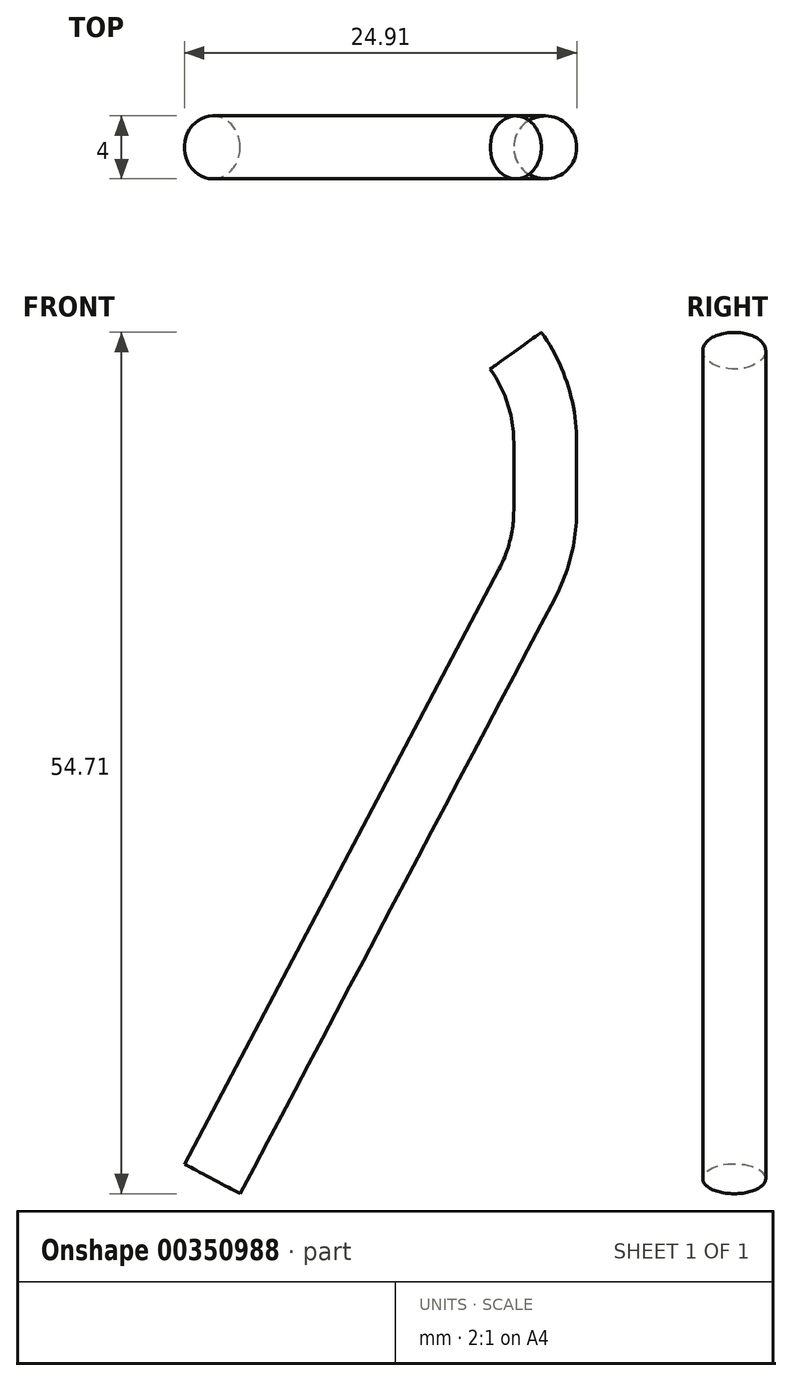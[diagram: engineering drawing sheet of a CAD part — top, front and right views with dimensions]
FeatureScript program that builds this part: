
annotation { "Feature Type Name" : "Feature", "Feature Type Description" : "" }
export const myFeature = defineFeature(function(context is Context, id is Id, definition is map)
    precondition{}
    {
        {
            var Q0;
            Q0=qCreatedBy(makeId("Front.planeOp"),FACE);
            var sketch = newSketch(context, id + "F0", { "sketchPlane" : qUnion([Q0])});
            skFitSpline(sketch, "E0.0", {"points": [v(10.89, 62.41) * mm, v(11.22, 61) * mm, v(11.72, 58.71) * mm, v(12.02, 56.72) * mm, v(12.14, 55.35) * mm, v(12.18, 54.52) * mm, v(12.19, 53.83) * mm, v(12.19, 53.1) * mm, v(12.18, 52.14) * mm, v(12.14, 50.91) * mm, v(12.08, 49.22) * mm, v(12, 47.68) * mm, v(11.94, 46.38) * mm, v(11.9, 45.51) * mm, v(11.84, 44.47) * mm, v(11.76, 43.28) * mm, v(11.6, 41.77) * mm, v(11.35, 40.39) * mm, v(10.94, 39.11) * mm, v(10.4, 37.86) * mm, v(9.46, 36.27) * mm, v(7.76, 34.27) * mm, v(5.42, 32.12) * mm, v(2.37, 29.78) * mm, v(-1.26, 27.28) * mm, v(-5.32, 24.6) * mm, v(-9.7, 21.74) * mm, v(-14.24, 18.69) * mm, v(-18.83, 15.43) * mm, v(-23.35, 11.96) * mm, v(-27.74, 8.21) * mm, v(-31.94, 4.17) * mm, v(-35.9, -0.22) * mm, v(-39.54, -5) * mm, v(-42.28, -9.32) * mm, v(-44.26, -13.01) * mm, v(-46.08, -16.86) * mm, v(-48.05, -21.95) * mm, v(-49.98, -28.38) * mm, v(-51.5, -35.06) * mm, v(-53.02, -44.16) * mm, v(-53.87, -53.38) * mm, v(-54.15, -61.23) * mm, v(-54.19, -65.6) * mm, v(-54.16, -69.9) * mm, v(-53.98, -75.09) * mm, v(-53.4, -83.12) * mm, v(-52.38, -90.88) * mm, v(-50.87, -98.64) * mm, v(-49.49, -104.51) * mm, v(-47.86, -110.52) * mm, v(-45.97, -116.72) * mm, v(-43.84, -123.1) * mm, v(-40.7, -131.75) * mm, v(-36.23, -142.78) * mm, v(-31.14, -153.78) * mm, v(-26.76, -162.4) * mm, v(-23.32, -168.72) * mm, v(-19.77, -174.87) * mm, v(-14.93, -182.84) * mm, v(-10, -190.44) * mm, v(-5.12, -197.65) * mm, v(-1.5, -202.86) * mm, v(2.01, -207.86) * mm, v(5.4, -212.65) * mm, v(8.65, -217.23) * mm, v(12.85, -223.12) * mm, v(17.87, -230.16) * mm, v(21.77, -235.6) * mm, v(23.72, -238.32) * mm]});
            skLineSegment(sketch, "E1", {"start": v(21.14, -237.93) * mm, "end": v(21.14, -242.24) * mm});
            skLineSegment(sketch, "E2", {"start": v(19.98, -246.9) * mm, "end": v(0, -284.72) * mm});
            skPoint(sketch, "E3.visualSharp", {"position": v(21.14, -234.72) * mm});
            skArc(sketch, "E3.filletArc", {"start": v(21.14, -237.93) * mm, "mid": v(20.66, -234.87) * mm, "end": v(19.27, -232.1) * mm});
            skPoint(sketch, "E4.visualSharp", {"position": v(21.14, -244.72) * mm});
            skArc(sketch, "E4.filletArc", {"start": v(19.98, -246.9) * mm, "mid": v(20.84, -244.64) * mm, "end": v(21.14, -242.24) * mm});
            skSolve(sketch);
        }
        {
            var Q0;
            Q0=sQuery(id+"F0.wireOp",VERTEX,"E0.0.start");
            var Q1;
            Q1=sQuery(id+"F0.wireOp",EDGE,"E0.0");
            cPlane(context, id + "F1", {"entities" : qUnion([Q0, Q1]), "cplaneType" : CPlaneType.CURVE_POINT, "offset" : 25 * mm, "width" : 150 * mm, "height" : 150 * mm});
        }
        {
            var Q0;
            Q0=qCreatedBy(id+"F1.planeOp",FACE);
            var sketch = newSketch(context, id + "F2", { "sketchPlane" : qUnion([Q0])});
            skCircle(sketch, "E5", {"center": v(25.09, 0) * mm, "radius": 2 * mm});
            skSolve(sketch);
        }
        {
            var Q0;
            Q0=sQuery(id+"F0.wireOp",EDGE,"E3.filletArc");
            var Q1;
            Q1=sQuery(id+"F0.wireOp",VERTEX,"E3.filletArc.end");
            cPlane(context, id + "F3", {"entities" : qUnion([Q0, Q1]), "cplaneType" : CPlaneType.CURVE_POINT, "offset" : 25 * mm, "width" : 150 * mm, "height" : 150 * mm});
        }
        {
            var Q0;
            Q0=qCreatedBy(id+"F3.planeOp",FACE);
            var sketch = newSketch(context, id + "F4", { "sketchPlane" : qUnion([Q0])});
            skCircle(sketch, "E6", {"center": v(-119.42, 0) * mm, "radius": 2 * mm});
            skSolve(sketch);
        }
        {
            var Q0;
            Q0 = qSketchRegion(id + "F4", true);
            var Q1;
            Q1=sQuery(id+"F0.wireOp",EDGE,"E3.filletArc");
            var Q2;
            Q2=sQuery(id+"F0.wireOp",EDGE,"E1");
            var Q3;
            Q3=sQuery(id+"F0.wireOp",EDGE,"E4.filletArc");
            var Q4;
            Q4=sQuery(id+"F0.wireOp",EDGE,"E2");
            sweep(context, id + "F5", {"profiles" : qUnion([Q0]), "path" : qUnion([Q1, Q2, Q3, Q4])});
        }
    });
